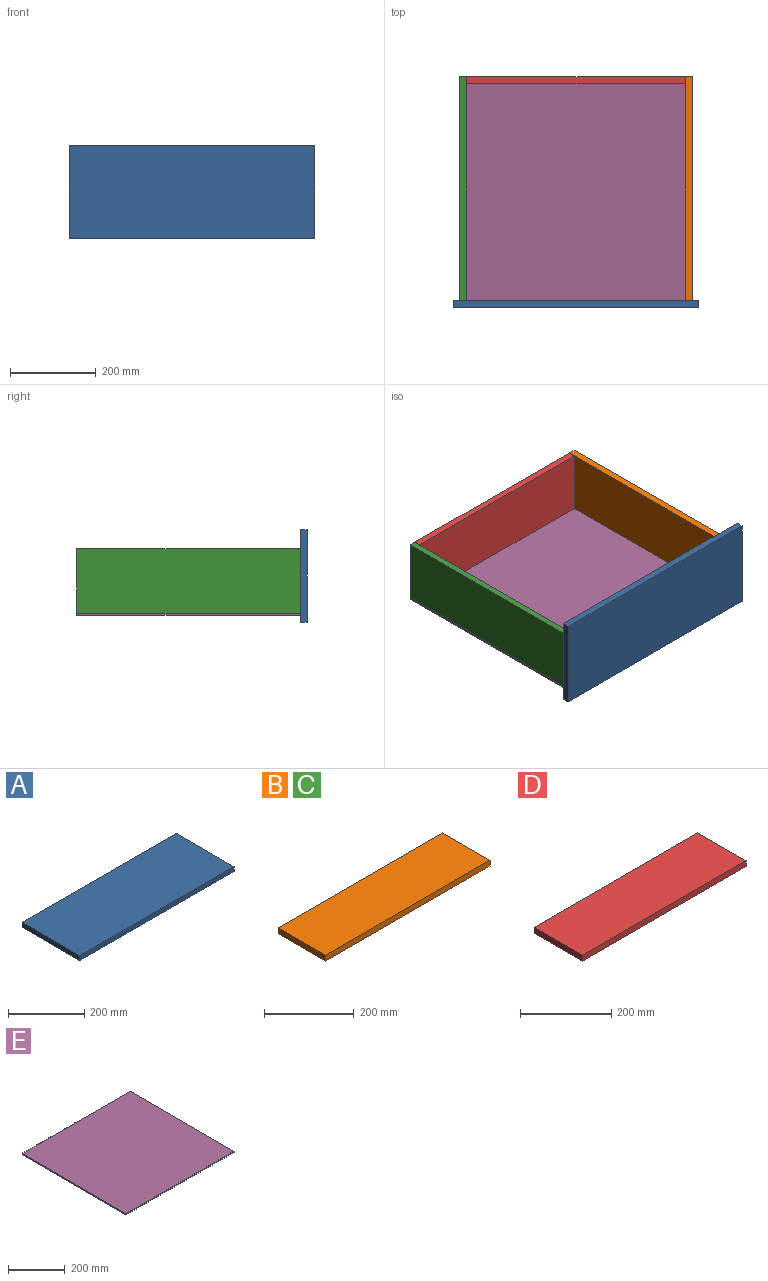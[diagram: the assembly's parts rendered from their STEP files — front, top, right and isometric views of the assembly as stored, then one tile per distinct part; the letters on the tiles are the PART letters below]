
ASSEMBLY  parts=5 mates=4
PART A: 6 faces, bbox 572x215x16 mm
  f0: plane 572x215mm, normal (0,0,-1), area 122980mm2, adj f1,f3,f4,f5
  f1: plane 215x16mm, normal (1,0,0), area 3440mm2, adj f0,f2,f4,f5
  f2: plane 572x215mm, normal (0,0,1), area 122980mm2, adj f1,f3,f4,f5
  f3: plane 215x16mm, normal (-1,0,0), area 3440mm2, adj f0,f2,f4,f5
  f4: plane 572x16mm, normal (0,-1,0), area 9152mm2, adj f0,f1,f2,f3
  f5: plane 572x16mm, normal (0,1,0), area 9152mm2, adj f0,f1,f2,f3
PART B: 6 faces, bbox 520x150x16 mm
  f0: plane 150x16mm, normal (1,0,0), area 2400mm2, adj f1,f3,f4,f5
  f1: plane 520x150mm, normal (0,0,1), area 78000mm2, adj f0,f2,f4,f5
  f2: plane 150x16mm, normal (-1,0,0), area 2400mm2, adj f1,f3,f4,f5
  f3: plane 520x150mm, normal (0,0,-1), area 78000mm2, adj f0,f2,f4,f5
  f4: plane 520x16mm, normal (0,-1,0), area 8320mm2, adj f0,f1,f2,f3
  f5: plane 520x16mm, normal (0,1,0), area 8320mm2, adj f0,f1,f2,f3
PART C: same geometry as B
PART D: 6 faces, bbox 508x150x16 mm
  f0: plane 508x150mm, normal (0,0,-1), area 76200mm2, adj f1,f3,f4,f5
  f1: plane 150x16mm, normal (1,0,0), area 2400mm2, adj f0,f2,f4,f5
  f2: plane 508x150mm, normal (0,0,1), area 76200mm2, adj f1,f3,f4,f5
  f3: plane 150x16mm, normal (-1,0,0), area 2400mm2, adj f0,f2,f4,f5
  f4: plane 508x16mm, normal (0,-1,0), area 8128mm2, adj f0,f1,f2,f3
  f5: plane 508x16mm, normal (0,1,0), area 8128mm2, adj f0,f1,f2,f3
PART E: 6 faces, bbox 540x520x5 mm
  f0: plane 520x5mm, normal (1,0,0), area 2600mm2, adj f1,f3,f4,f5
  f1: plane 540x520mm, normal (0,0,1), area 280800mm2, adj f0,f2,f4,f5
  f2: plane 520x5mm, normal (-1,0,0), area 2600mm2, adj f1,f3,f4,f5
  f3: plane 540x520mm, normal (0,0,-1), area 280800mm2, adj f0,f2,f4,f5
  f4: plane 540x5mm, normal (0,1,0), area 2700mm2, adj f0,f1,f2,f3
  f5: plane 540x5mm, normal (0,-1,0), area 2700mm2, adj f0,f1,f2,f3
PLACE A rot(axis=(1,0,0),90deg) t=(-91.5,2302.32,215)mm fixed
PLACE B rot(axis=(0.58,-0.58,-0.58),120deg) t=(2672.27,637.5,171)mm
PLACE C rot(axis=(-0.58,-0.58,0.58),120deg) t=(2148.27,-117.5,21)mm
PLACE D rot(axis=(1,0,0),90deg) t=(-91.5,2444.43,171)mm
PLACE E rot(axis=(-1,0,0),0deg) t=(-91.5,520,-1514.8)mm
MATE fastened C.f2 <-> A.f0  axis (0,-1,0) through (16,0,96)mm
MATE fastened C.f5 <-> E.f1  axis (0,0,-1) through (16,260,21)mm
MATE fastened D.f1 <-> B.f1  axis (1,0,0) through (540,520,96)mm
MATE fastened D.f3 <-> C.f3  axis (-1,0,0) through (32,520,96)mm
